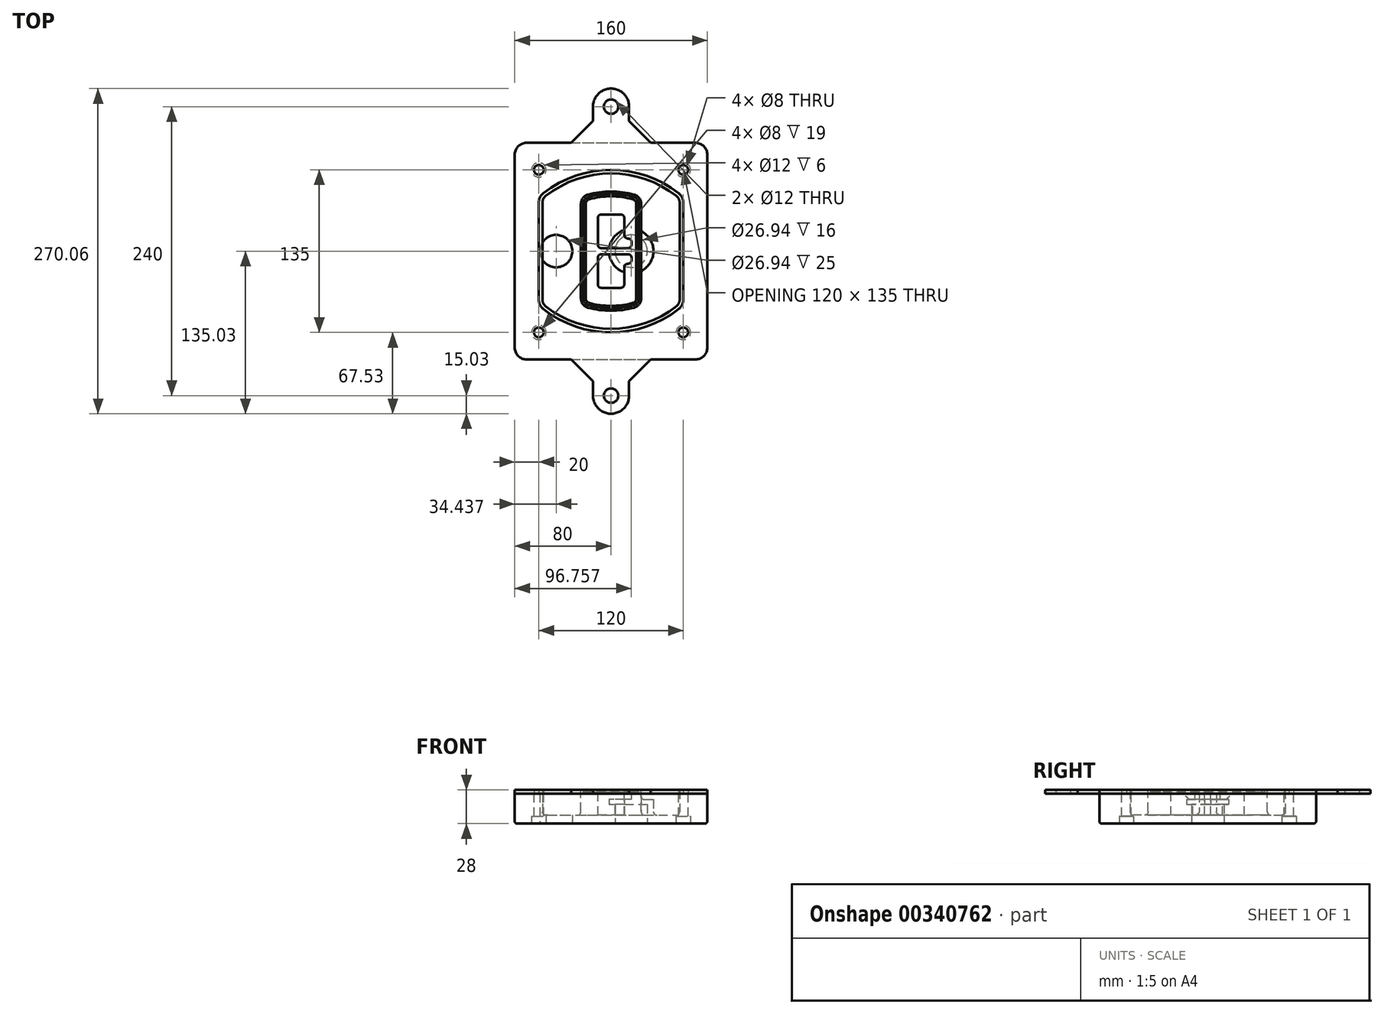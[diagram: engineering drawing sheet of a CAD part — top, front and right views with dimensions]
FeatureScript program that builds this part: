
annotation { "Feature Type Name" : "Feature", "Feature Type Description" : "" }
export const myFeature = defineFeature(function(context is Context, id is Id, definition is map)
    precondition{}
    {
        {
            var Q0;
            Q0=qCreatedBy(makeId("Top.planeOp"),FACE);
            var sketch = newSketch(context, id + "F0", { "sketchPlane" : qUnion([Q0])});
            skPoint(sketch, "E0.rect.middle", {"position": v(0, 0) * mm});
            skLineSegment(sketch, "E1.bottom", {"start": v(-70, -90) * mm, "end": v(70, -90) * mm});
            skLineSegment(sketch, "E1.top", {"start": v(-70, 90) * mm, "end": v(70, 90) * mm});
            skLineSegment(sketch, "E1.left", {"start": v(-80, -80) * mm, "end": v(-80, 80) * mm});
            skLineSegment(sketch, "E1.right", {"start": v(80, -80) * mm, "end": v(80, 80) * mm});
            skLineSegment(sketch, "E2", {"start": v(-80, 90) * mm, "end": v(80, -90) * mm, "construction": true});
            skLineSegment(sketch, "E3", {"start": v(80, 90) * mm, "end": v(-80, -90) * mm, "construction": true});
            skCircle(sketch, "E4", {"center": v(-60, 67.5) * mm, "radius": 4 * mm});
            skCircle(sketch, "E5", {"center": v(60, 67.5) * mm, "radius": 4 * mm});
            skCircle(sketch, "E6", {"center": v(60, -67.5) * mm, "radius": 4 * mm});
            skCircle(sketch, "E7", {"center": v(-60, -67.5) * mm, "radius": 4 * mm});
            skLineSegment(sketch, "E8", {"start": v(-60, 67.5) * mm, "end": v(60, 67.5) * mm, "construction": true});
            skLineSegment(sketch, "E9", {"start": v(60, 67.5) * mm, "end": v(60, -67.5) * mm, "construction": true});
            skLineSegment(sketch, "E10", {"start": v(60, -67.5) * mm, "end": v(-60, -67.5) * mm, "construction": true});
            skLineSegment(sketch, "E11", {"start": v(-60, -67.5) * mm, "end": v(-60, 67.5) * mm, "construction": true});
            skLineSegment(sketch, "E12", {"start": v(-60, 40.3) * mm, "end": v(-60, -40.3) * mm});
            skLineSegment(sketch, "E13", {"start": v(60, 40.3) * mm, "end": v(60, -40.3) * mm});
            skArc(sketch, "E14", {"start": v(56.15, 48.18) * mm, "mid": v(0, 67.5) * mm, "end": v(-56.15, 48.18) * mm});
            skArc(sketch, "E15", {"start": v(-56.15, -48.18) * mm, "mid": v(0, -67.5) * mm, "end": v(56.15, -48.18) * mm});
            skLineSegment(sketch, "E16", {"start": v(-60, 0) * mm, "end": v(60, 0) * mm, "construction": true});
            skPoint(sketch, "E17.visualSharp", {"position": v(-60, -45) * mm});
            skArc(sketch, "E17.filletArc", {"start": v(-60, -40.3) * mm, "mid": v(-58.99, -44.68) * mm, "end": v(-56.15, -48.18) * mm});
            skPoint(sketch, "E18.visualSharp", {"position": v(-60, 45) * mm});
            skArc(sketch, "E18.filletArc", {"start": v(-56.15, 48.18) * mm, "mid": v(-58.99, 44.68) * mm, "end": v(-60, 40.3) * mm});
            skPoint(sketch, "E19.visualSharp", {"position": v(60, 45) * mm});
            skArc(sketch, "E19.filletArc", {"start": v(60, 40.3) * mm, "mid": v(58.99, 44.68) * mm, "end": v(56.15, 48.18) * mm});
            skPoint(sketch, "E20.visualSharp", {"position": v(60, -45) * mm});
            skArc(sketch, "E20.filletArc", {"start": v(56.15, -48.18) * mm, "mid": v(58.99, -44.68) * mm, "end": v(60, -40.3) * mm});
            skPoint(sketch, "E21.visualSharp", {"position": v(-80, 90) * mm});
            skArc(sketch, "E21.filletArc", {"start": v(-70, 90) * mm, "mid": v(-77.07, 87.07) * mm, "end": v(-80, 80) * mm});
            skPoint(sketch, "E22.visualSharp", {"position": v(80, 90) * mm});
            skArc(sketch, "E22.filletArc", {"start": v(80, 80) * mm, "mid": v(77.07, 87.07) * mm, "end": v(70, 90) * mm});
            skPoint(sketch, "E23.visualSharp", {"position": v(80, -90) * mm});
            skArc(sketch, "E23.filletArc", {"start": v(70, -90) * mm, "mid": v(77.07, -87.07) * mm, "end": v(80, -80) * mm});
            skPoint(sketch, "E24.visualSharp", {"position": v(-80, -90) * mm});
            skArc(sketch, "E24.filletArc", {"start": v(-80, -80) * mm, "mid": v(-77.07, -87.07) * mm, "end": v(-70, -90) * mm});
            skArc(sketch, "E25.0", {"start": v(57, 40.3) * mm, "mid": v(56.3, 43.36) * mm, "end": v(54.3, 45.81) * mm});
            skLineSegment(sketch, "E25.1", {"start": v(57, 40.3) * mm, "end": v(57, -40.3) * mm});
            skArc(sketch, "E25.2", {"start": v(54.3, -45.81) * mm, "mid": v(56.3, -43.36) * mm, "end": v(57, -40.3) * mm});
            skArc(sketch, "E25.3", {"start": v(-54.3, -45.81) * mm, "mid": v(0, -64.5) * mm, "end": v(54.3, -45.81) * mm});
            skArc(sketch, "E25.4", {"start": v(-57, -40.3) * mm, "mid": v(-56.3, -43.36) * mm, "end": v(-54.3, -45.81) * mm});
            skArc(sketch, "E25.5", {"start": v(54.3, 45.81) * mm, "mid": v(0, 64.5) * mm, "end": v(-54.3, 45.81) * mm});
            skLineSegment(sketch, "E25.6", {"start": v(-57, 40.3) * mm, "end": v(-57, -40.3) * mm});
            skArc(sketch, "E25.7", {"start": v(-54.3, 45.81) * mm, "mid": v(-56.3, 43.36) * mm, "end": v(-57, 40.3) * mm});
            skArc(sketch, "E26.0", {"start": v(-58.62, 51.33) * mm, "mid": v(-62.58, 46.43) * mm, "end": v(-64, 40.3) * mm});
            skArc(sketch, "E26.1", {"start": v(58.62, 51.33) * mm, "mid": v(0, 71.5) * mm, "end": v(-58.62, 51.33) * mm});
            skArc(sketch, "E26.2", {"start": v(64, 40.3) * mm, "mid": v(62.58, 46.43) * mm, "end": v(58.62, 51.33) * mm});
            skLineSegment(sketch, "E26.3", {"start": v(64, 40.3) * mm, "end": v(64, -40.3) * mm});
            skArc(sketch, "E26.4", {"start": v(58.62, -51.33) * mm, "mid": v(62.58, -46.43) * mm, "end": v(64, -40.3) * mm});
            skLineSegment(sketch, "E26.5", {"start": v(-64, 40.3) * mm, "end": v(-64, -40.3) * mm});
            skArc(sketch, "E26.6", {"start": v(-58.62, -51.33) * mm, "mid": v(0, -71.5) * mm, "end": v(58.62, -51.33) * mm});
            skArc(sketch, "E26.7", {"start": v(-64, -40.3) * mm, "mid": v(-62.58, -46.43) * mm, "end": v(-58.62, -51.33) * mm});
            skSolve(sketch);
        }
        {
            var Q0;
            Q0=makeQuery(id+"F0.imprint","IMPRINT",FACE,{"disambiguationData":[TD([[makeQuery(id+"F0.imprint","IMPRINT",EDGE,{"derivedFrom":sQuery(id+"F0.wireOp",EDGE,"E1.bottom")}),1.0]])]});
            var Q1;
            Q1=makeQuery(id+"F0.imprint","IMPRINT",FACE,{"disambiguationData":[TD([[makeQuery(id+"F0.imprint","IMPRINT",EDGE,{"derivedFrom":sQuery(id+"F0.wireOp",EDGE,"E12")}),1.0]])]});
            var Q2;
            Q2=makeQuery(id+"F0.imprint","IMPRINT",FACE,{"disambiguationData":[TD([[makeQuery(id+"F0.imprint","IMPRINT",EDGE,{"derivedFrom":sQuery(id+"F0.wireOp",EDGE,"E25.0")}),1.0]])]});
            var Q3;
            Q3=makeQuery(id+"F0.imprint","IMPRINT",FACE,{"disambiguationData":[TD([[makeQuery(id+"F0.imprint","IMPRINT",EDGE,{"derivedFrom":sQuery(id+"F0.wireOp",EDGE,"E12")}),-1.0]])]});
            extrude(context, id + "F1", {"entities" : qUnion([Q0, Q1, Q2, Q3]), "oppositeDirection" : true, "depth" : 25 * mm});
        }
        {
            var Q0;
            Q0=makeQuery(id+"F0.imprint","IMPRINT",FACE,{"disambiguationData":[TD([[makeQuery(id+"F0.imprint","IMPRINT",EDGE,{"derivedFrom":sQuery(id+"F0.wireOp",EDGE,"E12")}),1.0]])]});
            extrude(context, id + "F2", {"entities" : qUnion([Q0]), "operationType" : NewBodyOperationType.ADD, "depth" : 3 * mm});
        }
        {
            var Q0;
            Q0=makeQuery(id+"F0.imprint","IMPRINT",FACE,{"disambiguationData":[TD([[makeQuery(id+"F0.imprint","IMPRINT",EDGE,{"derivedFrom":sQuery(id+"F0.wireOp",EDGE,"E25.0")}),1.0]])]});
            extrude(context, id + "F3", {"entities" : qUnion([Q0]), "operationType" : NewBodyOperationType.REMOVE, "oppositeDirection" : true, "depth" : 18 * mm});
        }
        {
            var Q0;
            Q0=makeQuery(id+"F2.opExtrude","CAP_FACE",FACE,{"disambiguationData":[OSD([sQuery(id+"F0.wireOp",EDGE,"E12"),sQuery(id+"F0.wireOp",EDGE,"E13"),sQuery(id+"F0.wireOp",EDGE,"E14"),sQuery(id+"F0.wireOp",EDGE,"E15"),sQuery(id+"F0.wireOp",EDGE,"E17.filletArc"),sQuery(id+"F0.wireOp",EDGE,"E18.filletArc"),sQuery(id+"F0.wireOp",EDGE,"E19.filletArc"),sQuery(id+"F0.wireOp",EDGE,"E20.filletArc"),sQuery(id+"F0.wireOp",EDGE,"E25.0"),sQuery(id+"F0.wireOp",EDGE,"E25.1"),sQuery(id+"F0.wireOp",EDGE,"E25.2"),sQuery(id+"F0.wireOp",EDGE,"E25.3"),sQuery(id+"F0.wireOp",EDGE,"E25.4"),sQuery(id+"F0.wireOp",EDGE,"E25.5"),sQuery(id+"F0.wireOp",EDGE,"E25.6"),sQuery(id+"F0.wireOp",EDGE,"E25.7")])],"isStart":false});
            var sketch = newSketch(context, id + "F4", { "sketchPlane" : qUnion([Q0])});
            skArc(sketch, "E27.0", {"start": v(-19.08, -46.97) * mm, "mid": v(0, -49.5) * mm, "end": v(19.08, -46.97) * mm});
            skArc(sketch, "E28.0", {"start": v(19.08, 46.97) * mm, "mid": v(0, 49.5) * mm, "end": v(-19.08, 46.97) * mm});
            skLineSegment(sketch, "E29", {"start": v(-25, 39.25) * mm, "end": v(-25, -39.25) * mm});
            skLineSegment(sketch, "E30", {"start": v(25, 39.25) * mm, "end": v(25, -39.25) * mm});
            skLineSegment(sketch, "E31", {"start": v(-25, 45.1) * mm, "end": v(25, 45.1) * mm, "construction": true});
            skLineSegment(sketch, "E32", {"start": v(-25, -45.1) * mm, "end": v(25, -45.1) * mm, "construction": true});
            skPoint(sketch, "E33.visualSharp", {"position": v(-25, 45.1) * mm});
            skArc(sketch, "E33.filletArc", {"start": v(-19.08, 46.97) * mm, "mid": v(-23.35, 44.11) * mm, "end": v(-25, 39.25) * mm});
            skPoint(sketch, "E34.visualSharp", {"position": v(25, 45.1) * mm});
            skArc(sketch, "E34.filletArc", {"start": v(25, 39.25) * mm, "mid": v(23.35, 44.11) * mm, "end": v(19.08, 46.97) * mm});
            skPoint(sketch, "E35.visualSharp", {"position": v(25, -45.1) * mm});
            skArc(sketch, "E35.filletArc", {"start": v(19.08, -46.97) * mm, "mid": v(23.35, -44.11) * mm, "end": v(25, -39.25) * mm});
            skPoint(sketch, "E36.visualSharp", {"position": v(-25, -45.1) * mm});
            skArc(sketch, "E36.filletArc", {"start": v(-25, -39.25) * mm, "mid": v(-23.35, -44.11) * mm, "end": v(-19.08, -46.97) * mm});
            skArc(sketch, "E37.0", {"start": v(54.3, 45.81) * mm, "mid": v(0, 64.5) * mm, "end": v(-54.3, 45.81) * mm});
            skArc(sketch, "E37.1", {"start": v(-54.3, 45.81) * mm, "mid": v(-56.3, 43.36) * mm, "end": v(-57, 40.3) * mm});
            skLineSegment(sketch, "E37.2", {"start": v(-57, 40.3) * mm, "end": v(-57, -40.3) * mm});
            skArc(sketch, "E37.3", {"start": v(-57, -40.3) * mm, "mid": v(-56.3, -43.36) * mm, "end": v(-54.3, -45.81) * mm});
            skArc(sketch, "E37.4", {"start": v(-54.3, -45.81) * mm, "mid": v(0, -64.5) * mm, "end": v(54.3, -45.81) * mm});
            skArc(sketch, "E37.5", {"start": v(54.3, -45.81) * mm, "mid": v(56.3, -43.36) * mm, "end": v(57, -40.3) * mm});
            skLineSegment(sketch, "E37.6", {"start": v(57, 40.3) * mm, "end": v(57, -40.3) * mm});
            skArc(sketch, "E37.7", {"start": v(57, 40.3) * mm, "mid": v(56.3, 43.36) * mm, "end": v(54.3, 45.81) * mm});
            skLineSegment(sketch, "E38.0", {"start": v(23, 39.25) * mm, "end": v(23, -39.25) * mm});
            skArc(sketch, "E38.1", {"start": v(18.56, -45.04) * mm, "mid": v(21.76, -42.9) * mm, "end": v(23, -39.25) * mm});
            skArc(sketch, "E38.2", {"start": v(-18.56, -45.04) * mm, "mid": v(0, -47.5) * mm, "end": v(18.56, -45.04) * mm});
            skArc(sketch, "E38.3", {"start": v(-23, -39.25) * mm, "mid": v(-21.76, -42.9) * mm, "end": v(-18.56, -45.04) * mm});
            skLineSegment(sketch, "E38.4", {"start": v(-23, 39.25) * mm, "end": v(-23, -39.25) * mm});
            skArc(sketch, "E38.5", {"start": v(23, 39.25) * mm, "mid": v(21.76, 42.9) * mm, "end": v(18.56, 45.04) * mm});
            skArc(sketch, "E38.6", {"start": v(-18.56, 45.04) * mm, "mid": v(-21.76, 42.9) * mm, "end": v(-23, 39.25) * mm});
            skArc(sketch, "E38.7", {"start": v(18.56, 45.04) * mm, "mid": v(0, 47.5) * mm, "end": v(-18.56, 45.04) * mm});
            skArc(sketch, "E39.0", {"start": v(21, 39.25) * mm, "mid": v(20.18, 41.68) * mm, "end": v(18.04, 43.1) * mm});
            skLineSegment(sketch, "E39.1", {"start": v(21, 39.25) * mm, "end": v(21, -39.25) * mm});
            skArc(sketch, "E39.2", {"start": v(18.04, -43.1) * mm, "mid": v(20.18, -41.68) * mm, "end": v(21, -39.25) * mm});
            skArc(sketch, "E39.3", {"start": v(-18.04, -43.1) * mm, "mid": v(0, -45.5) * mm, "end": v(18.04, -43.1) * mm});
            skArc(sketch, "E39.4", {"start": v(-21, -39.25) * mm, "mid": v(-20.18, -41.68) * mm, "end": v(-18.04, -43.1) * mm});
            skArc(sketch, "E39.5", {"start": v(18.04, 43.1) * mm, "mid": v(0, 45.5) * mm, "end": v(-18.04, 43.1) * mm});
            skLineSegment(sketch, "E39.6", {"start": v(-21, 39.25) * mm, "end": v(-21, -39.25) * mm});
            skArc(sketch, "E39.7", {"start": v(-18.04, 43.1) * mm, "mid": v(-20.18, 41.68) * mm, "end": v(-21, 39.25) * mm});
            skLineSegment(sketch, "E40", {"start": v(-25, 0) * mm, "end": v(25, 0) * mm, "construction": true});
            skLineSegment(sketch, "E41", {"start": v(-11, 5.5) * mm, "end": v(-11, 27.5) * mm});
            skLineSegment(sketch, "E42", {"start": v(-8, 30.5) * mm, "end": v(8, 30.5) * mm});
            skLineSegment(sketch, "E43", {"start": v(11, 27.5) * mm, "end": v(11, 13.5) * mm});
            skLineSegment(sketch, "E44", {"start": v(14, 10.5) * mm, "end": v(14, 10.5) * mm});
            skLineSegment(sketch, "E45", {"start": v(17, 7.5) * mm, "end": v(17, 5.5) * mm});
            skLineSegment(sketch, "E46", {"start": v(14, 2.5) * mm, "end": v(-8, 2.5) * mm});
            skPoint(sketch, "E47.visualSharp", {"position": v(-11, 30.5) * mm});
            skArc(sketch, "E47.filletArc", {"start": v(-8, 30.5) * mm, "mid": v(-10.12, 29.62) * mm, "end": v(-11, 27.5) * mm});
            skPoint(sketch, "E48.visualSharp", {"position": v(11, 30.5) * mm});
            skArc(sketch, "E48.filletArc", {"start": v(11, 27.5) * mm, "mid": v(10.12, 29.62) * mm, "end": v(8, 30.5) * mm});
            skPoint(sketch, "E49.visualSharp", {"position": v(11, 10.5) * mm});
            skArc(sketch, "E49.filletArc", {"start": v(11, 13.5) * mm, "mid": v(11.88, 11.38) * mm, "end": v(14, 10.5) * mm});
            skPoint(sketch, "E50.visualSharp", {"position": v(17, 10.5) * mm});
            skArc(sketch, "E50.filletArc", {"start": v(17, 7.5) * mm, "mid": v(16.12, 9.62) * mm, "end": v(14, 10.5) * mm});
            skPoint(sketch, "E51.visualSharp", {"position": v(17, 2.5) * mm});
            skArc(sketch, "E51.filletArc", {"start": v(14, 2.5) * mm, "mid": v(16.12, 3.38) * mm, "end": v(17, 5.5) * mm});
            skPoint(sketch, "E52.visualSharp", {"position": v(-11, 2.5) * mm});
            skArc(sketch, "E52.filletArc", {"start": v(-11, 5.5) * mm, "mid": v(-10.12, 3.38) * mm, "end": v(-8, 2.5) * mm});
            skLineSegment(sketch, "E53.0.MirrorCS", {"start": v(14, -2.5) * mm, "end": v(-8, -2.5) * mm});
            skArc(sketch, "E54.0.MirrorCS", {"start": v(-11, -5.5) * mm, "mid": v(-10.12, -3.38) * mm, "end": v(-8, -2.5) * mm});
            skLineSegment(sketch, "E55.0.MirrorCS", {"start": v(-11, -5.5) * mm, "end": v(-11, -27.5) * mm});
            skArc(sketch, "E56.0.MirrorCS", {"start": v(-8, -30.5) * mm, "mid": v(-10.12, -29.62) * mm, "end": v(-11, -27.5) * mm});
            skLineSegment(sketch, "E57.0.MirrorCS", {"start": v(-8, -30.5) * mm, "end": v(8, -30.5) * mm});
            skArc(sketch, "E58.0.MirrorCS", {"start": v(11, -27.5) * mm, "mid": v(10.12, -29.62) * mm, "end": v(8, -30.5) * mm});
            skLineSegment(sketch, "E59.0.MirrorCS", {"start": v(11, -27.5) * mm, "end": v(11, -13.5) * mm});
            skArc(sketch, "E60.0.MirrorCS", {"start": v(11, -13.5) * mm, "mid": v(11.88, -11.38) * mm, "end": v(14, -10.5) * mm});
            skArc(sketch, "E61.0.MirrorCS", {"start": v(17, -7.5) * mm, "mid": v(16.12, -9.62) * mm, "end": v(14, -10.5) * mm});
            skLineSegment(sketch, "E62.0.MirrorCS", {"start": v(17, -7.5) * mm, "end": v(17, -5.5) * mm});
            skArc(sketch, "E63.0.MirrorCS", {"start": v(14, -2.5) * mm, "mid": v(16.12, -3.38) * mm, "end": v(17, -5.5) * mm});
            skSolve(sketch);
        }
        {
            var Q0;
            Q0=makeQuery(id+"F4.imprint","IMPRINT",FACE,{"disambiguationData":[TD([[makeQuery(id+"F4.imprint","IMPRINT",EDGE,{"derivedFrom":sQuery(id+"F4.wireOp",EDGE,"E27.0")}),1.0]])]});
            var Q1;
            Q1=makeQuery(id+"F4.imprint","IMPRINT",FACE,{"disambiguationData":[TD([[makeQuery(id+"F4.imprint","IMPRINT",EDGE,{"derivedFrom":sQuery(id+"F4.wireOp",EDGE,"E38.0")}),-1.0]])]});
            var Q2;
            Q2=makeQuery(id+"F4.imprint","IMPRINT",FACE,{"disambiguationData":[TD([[makeQuery(id+"F4.imprint","IMPRINT",EDGE,{"derivedFrom":sQuery(id+"F4.wireOp",EDGE,"E39.0")}),1.0]])]});
            extrude(context, id + "F5", {"entities" : qUnion([Q0, Q1, Q2]), "operationType" : NewBodyOperationType.ADD, "endBound" : BoundingType.UP_TO_NEXT, "oppositeDirection" : true, "depth" : 25 * mm});
        }
        {
            var Q0;
            Q0=makeQuery(id+"F4.imprint","IMPRINT",FACE,{"disambiguationData":[TD([[makeQuery(id+"F4.imprint","IMPRINT",EDGE,{"derivedFrom":sQuery(id+"F4.wireOp",EDGE,"E38.0")}),-1.0]])]});
            extrude(context, id + "F6", {"entities" : qUnion([Q0]), "operationType" : NewBodyOperationType.REMOVE, "oppositeDirection" : true, "depth" : 2 * mm});
        }
        {
            var Q0;
            Q0=makeQuery(id+"F1.opExtrude","CAP_FACE",FACE,{"disambiguationData":[OSD([sQuery(id+"F0.wireOp",EDGE,"E1.bottom"),sQuery(id+"F0.wireOp",EDGE,"E1.top"),sQuery(id+"F0.wireOp",EDGE,"E1.left"),sQuery(id+"F0.wireOp",EDGE,"E1.right"),sQuery(id+"F0.wireOp",EDGE,"E4"),sQuery(id+"F0.wireOp",EDGE,"E5"),sQuery(id+"F0.wireOp",EDGE,"E6"),sQuery(id+"F0.wireOp",EDGE,"E7"),sQuery(id+"F0.wireOp",EDGE,"E21.filletArc"),sQuery(id+"F0.wireOp",EDGE,"E22.filletArc"),sQuery(id+"F0.wireOp",EDGE,"E23.filletArc"),sQuery(id+"F0.wireOp",EDGE,"E24.filletArc")])],"isStart":false});
            var sketch = newSketch(context, id + "F7", { "sketchPlane" : qUnion([Q0])});
            skCircle(sketch, "E64", {"center": v(16.76, 0) * mm, "radius": 13.47 * mm});
            skCircle(sketch, "E65", {"center": v(-45.56, 0) * mm, "radius": 13.47 * mm});
            skLineSegment(sketch, "E66", {"start": v(80, 0) * mm, "end": v(-80, 0) * mm});
            skCircle(sketch, "E67", {"center": v(16.76, 0) * mm, "radius": 18.47 * mm});
            skCircle(sketch, "E68", {"center": v(60, -67.5) * mm, "radius": 6 * mm});
            skCircle(sketch, "E69", {"center": v(-60, -67.5) * mm, "radius": 6 * mm});
            skCircle(sketch, "E70", {"center": v(-60, 67.5) * mm, "radius": 6 * mm});
            skCircle(sketch, "E71", {"center": v(60, 67.5) * mm, "radius": 6 * mm});
            skSolve(sketch);
        }
        {
            var Q0;
            {var subQ1=sQuery(id+"F7.wireOp",EDGE,"E66");var subQ4=sQuery(id+"F7.wireOp",EDGE,"E64");var subQ6=makeQuery(id+"F7.imprint","INTERSECT",VERTEX,{"disambiguationData":[OD(0.0)],"derivedFrom":[subQ4,subQ1]});Q0=makeQuery(id+"F7.imprint","IMPRINT",FACE,{"disambiguationData":[TD([[makeQuery(id+"F7.imprint","IMPRINT",EDGE,{"disambiguationData":[TD([[subQ6,-1.0]])],"derivedFrom":subQ4}),-1.0]])]});}
            var Q1;
            {var subQ0=sQuery(id+"F7.wireOp",EDGE,"E66");var subQ1=sQuery(id+"F7.wireOp",EDGE,"E64");var subQ3=makeQuery(id+"F7.imprint","INTERSECT",VERTEX,{"disambiguationData":[OD(0.0)],"derivedFrom":[subQ1,subQ0]});Q1=makeQuery(id+"F7.imprint","IMPRINT",FACE,{"disambiguationData":[TD([[makeQuery(id+"F7.imprint","IMPRINT",EDGE,{"disambiguationData":[TD([[subQ3,-1.0]])],"derivedFrom":subQ1}),1.0]])]});}
            var Q2;
            {var subQ0=sQuery(id+"F7.wireOp",EDGE,"E66");var subQ1=sQuery(id+"F7.wireOp",EDGE,"E64");var subQ3=makeQuery(id+"F7.imprint","INTERSECT",VERTEX,{"disambiguationData":[OD(0.0)],"derivedFrom":[subQ1,subQ0]});Q2=makeQuery(id+"F7.imprint","IMPRINT",FACE,{"disambiguationData":[TD([[makeQuery(id+"F7.imprint","IMPRINT",EDGE,{"disambiguationData":[TD([[subQ3,1.0]])],"derivedFrom":subQ1}),1.0]])]});}
            var Q3;
            {var subQ1=sQuery(id+"F7.wireOp",EDGE,"E66");var subQ4=sQuery(id+"F7.wireOp",EDGE,"E64");var subQ6=makeQuery(id+"F7.imprint","INTERSECT",VERTEX,{"disambiguationData":[OD(0.0)],"derivedFrom":[subQ4,subQ1]});Q3=makeQuery(id+"F7.imprint","IMPRINT",FACE,{"disambiguationData":[TD([[makeQuery(id+"F7.imprint","IMPRINT",EDGE,{"disambiguationData":[TD([[subQ6,1.0]])],"derivedFrom":subQ4}),-1.0]])]});}
            extrude(context, id + "F8", {"entities" : qUnion([Q0, Q1, Q2, Q3]), "operationType" : NewBodyOperationType.ADD, "oppositeDirection" : true, "depth" : 20 * mm});
        }
        {
            var Q0;
            {var subQ0=sQuery(id+"F7.wireOp",EDGE,"E66");var subQ1=sQuery(id+"F7.wireOp",EDGE,"E64");var subQ3=makeQuery(id+"F7.imprint","INTERSECT",VERTEX,{"disambiguationData":[OD(0.0)],"derivedFrom":[subQ1,subQ0]});Q0=makeQuery(id+"F7.imprint","IMPRINT",FACE,{"disambiguationData":[TD([[makeQuery(id+"F7.imprint","IMPRINT",EDGE,{"disambiguationData":[TD([[subQ3,-1.0]])],"derivedFrom":subQ1}),1.0]])]});}
            var Q1;
            {var subQ0=sQuery(id+"F7.wireOp",EDGE,"E66");var subQ1=sQuery(id+"F7.wireOp",EDGE,"E64");var subQ3=makeQuery(id+"F7.imprint","INTERSECT",VERTEX,{"disambiguationData":[OD(0.0)],"derivedFrom":[subQ1,subQ0]});Q1=makeQuery(id+"F7.imprint","IMPRINT",FACE,{"disambiguationData":[TD([[makeQuery(id+"F7.imprint","IMPRINT",EDGE,{"disambiguationData":[TD([[subQ3,1.0]])],"derivedFrom":subQ1}),1.0]])]});}
            extrude(context, id + "F9", {"entities" : qUnion([Q0, Q1]), "operationType" : NewBodyOperationType.REMOVE, "oppositeDirection" : true, "depth" : 16 * mm});
        }
        {
            var Q0;
            {var subQ0=sQuery(id+"F7.wireOp",EDGE,"E66");var subQ1=sQuery(id+"F7.wireOp",EDGE,"E65");var subQ3=makeQuery(id+"F7.imprint","INTERSECT",VERTEX,{"disambiguationData":[OD(0.0)],"derivedFrom":[subQ1,subQ0]});Q0=makeQuery(id+"F7.imprint","IMPRINT",FACE,{"disambiguationData":[TD([[makeQuery(id+"F7.imprint","IMPRINT",EDGE,{"disambiguationData":[TD([[subQ3,-1.0]])],"derivedFrom":subQ1}),1.0]])]});}
            var Q1;
            {var subQ0=sQuery(id+"F7.wireOp",EDGE,"E66");var subQ1=sQuery(id+"F7.wireOp",EDGE,"E65");var subQ3=makeQuery(id+"F7.imprint","INTERSECT",VERTEX,{"disambiguationData":[OD(0.0)],"derivedFrom":[subQ1,subQ0]});Q1=makeQuery(id+"F7.imprint","IMPRINT",FACE,{"disambiguationData":[TD([[makeQuery(id+"F7.imprint","IMPRINT",EDGE,{"disambiguationData":[TD([[subQ3,1.0]])],"derivedFrom":subQ1}),1.0]])]});}
            extrude(context, id + "F10", {"entities" : qUnion([Q0, Q1]), "operationType" : NewBodyOperationType.REMOVE, "oppositeDirection" : true, "depth" : 25 * mm});
        }
        {
            var Q0;
            Q0=makeQuery(id+"F7.imprint","IMPRINT",FACE,{"disambiguationData":[TD([[makeQuery(id+"F7.imprint","IMPRINT",EDGE,{"derivedFrom":sQuery(id+"F7.wireOp",EDGE,"E68")}),1.0]])]});
            var Q1;
            Q1=makeQuery(id+"F7.imprint","IMPRINT",FACE,{"disambiguationData":[TD([[makeQuery(id+"F7.imprint","IMPRINT",EDGE,{"derivedFrom":makeQuery(id+"F1.opExtrude","CAP_EDGE",EDGE,{"disambiguationData":[OSD([sQuery(id+"F0.wireOp",EDGE,"E5")])],"isStart":false})}),-1.0]])]});
            var Q2;
            Q2=makeQuery(id+"F7.imprint","IMPRINT",FACE,{"disambiguationData":[TD([[makeQuery(id+"F7.imprint","IMPRINT",EDGE,{"derivedFrom":sQuery(id+"F7.wireOp",EDGE,"E69")}),1.0]])]});
            var Q3;
            Q3=makeQuery(id+"F7.imprint","IMPRINT",FACE,{"disambiguationData":[TD([[makeQuery(id+"F7.imprint","IMPRINT",EDGE,{"derivedFrom":makeQuery(id+"F1.opExtrude","CAP_EDGE",EDGE,{"disambiguationData":[OSD([sQuery(id+"F0.wireOp",EDGE,"E4")])],"isStart":false})}),-1.0]])]});
            var Q4;
            Q4=makeQuery(id+"F7.imprint","IMPRINT",FACE,{"disambiguationData":[TD([[makeQuery(id+"F7.imprint","IMPRINT",EDGE,{"derivedFrom":sQuery(id+"F7.wireOp",EDGE,"E70")}),1.0]])]});
            var Q5;
            Q5=makeQuery(id+"F7.imprint","IMPRINT",FACE,{"disambiguationData":[TD([[makeQuery(id+"F7.imprint","IMPRINT",EDGE,{"derivedFrom":makeQuery(id+"F1.opExtrude","CAP_EDGE",EDGE,{"disambiguationData":[OSD([sQuery(id+"F0.wireOp",EDGE,"E7")])],"isStart":false})}),-1.0]])]});
            var Q6;
            Q6=makeQuery(id+"F7.imprint","IMPRINT",FACE,{"disambiguationData":[TD([[makeQuery(id+"F7.imprint","IMPRINT",EDGE,{"derivedFrom":sQuery(id+"F7.wireOp",EDGE,"E71")}),1.0]])]});
            var Q7;
            Q7=makeQuery(id+"F7.imprint","IMPRINT",FACE,{"disambiguationData":[TD([[makeQuery(id+"F7.imprint","IMPRINT",EDGE,{"derivedFrom":makeQuery(id+"F1.opExtrude","CAP_EDGE",EDGE,{"disambiguationData":[OSD([sQuery(id+"F0.wireOp",EDGE,"E6")])],"isStart":false})}),-1.0]])]});
            extrude(context, id + "F11", {"entities" : qUnion([Q0, Q1, Q2, Q3, Q4, Q5, Q6, Q7]), "operationType" : NewBodyOperationType.REMOVE, "oppositeDirection" : true, "depth" : 6 * mm});
        }
        {
            var Q0;
            Q0=makeQuery(id+"F9.boolean.opBoolean","COPY",FACE,{"derivedFrom":makeQuery(id+"F9.opExtrude","CAP_FACE",FACE,{"disambiguationData":[OSD([sQuery(id+"F7.wireOp",EDGE,"E64")])],"isStart":false})});
            var sketch = newSketch(context, id + "F12", { "sketchPlane" : qUnion([Q0])});
            skArc(sketch, "E72.0", {"start": v(11, 17.55) * mm, "mid": v(2.57, 11.82) * mm, "end": v(-1.54, 2.5) * mm});
            skArc(sketch, "E72.1", {"start": v(-1.54, -2.5) * mm, "mid": v(2.57, -11.82) * mm, "end": v(11, -17.55) * mm});
            skLineSegment(sketch, "E73", {"start": v(-1.54, -2.5) * mm, "end": v(14, -2.5) * mm});
            skLineSegment(sketch, "E74.0", {"start": v(14, 2.5) * mm, "end": v(-1.54, 2.5) * mm});
            skArc(sketch, "E74.1", {"start": v(14, 2.5) * mm, "mid": v(16.12, 3.38) * mm, "end": v(17, 5.5) * mm});
            skLineSegment(sketch, "E74.2", {"start": v(17, 7.5) * mm, "end": v(17, 5.5) * mm});
            skArc(sketch, "E74.3", {"start": v(17, 7.5) * mm, "mid": v(16.12, 9.62) * mm, "end": v(14, 10.5) * mm});
            skArc(sketch, "E74.4", {"start": v(11, 13.5) * mm, "mid": v(11.88, 11.38) * mm, "end": v(14, 10.5) * mm});
            skLineSegment(sketch, "E74.5", {"start": v(11, 17.55) * mm, "end": v(11, 13.5) * mm});
            skLineSegment(sketch, "E74.7", {"start": v(14, -2.5) * mm, "end": v(-1.54, -2.5) * mm});
            skArc(sketch, "E74.8", {"start": v(14, -2.5) * mm, "mid": v(16.12, -3.38) * mm, "end": v(17, -5.5) * mm});
            skLineSegment(sketch, "E74.9", {"start": v(17, -7.5) * mm, "end": v(17, -5.5) * mm});
            skArc(sketch, "E74.10", {"start": v(17, -7.5) * mm, "mid": v(16.12, -9.62) * mm, "end": v(14, -10.5) * mm});
            skArc(sketch, "E74.11", {"start": v(11, -13.5) * mm, "mid": v(11.88, -11.38) * mm, "end": v(14, -10.5) * mm});
            skLineSegment(sketch, "E74.12", {"start": v(11, -17.55) * mm, "end": v(11, -13.5) * mm});
            skPoint(sketch, "E75.orphan", {"position": v(11, -27.5) * mm});
            skPoint(sketch, "E76.orphan", {"position": v(-8, -2.5) * mm});
            skPoint(sketch, "E77.orphan", {"position": v(-8, 2.5) * mm});
            skPoint(sketch, "E78.orphan", {"position": v(11, 27.5) * mm});
            skSolve(sketch);
        }
        {
            var Q0;
            {var subQ7=sQuery(id+"F12.wireOp",EDGE,"E72.0");var subQ14=sQuery(id+"F12.wireOp",EDGE,"E72.1");var subQ16=sQuery(id+"F12.wireOp",EDGE,"E74.1");var subQ18=sQuery(id+"F12.wireOp",EDGE,"E74.8");Q0=qUnion([makeQuery(id+"F12.imprint","IMPRINT",FACE,{"disambiguationData":[TD([[makeQuery(id+"F12.imprint","IMPRINT",EDGE,{"derivedFrom":subQ7}),1.0]])]}),makeQuery(id+"F12.imprint","IMPRINT",FACE,{"disambiguationData":[TD([[makeQuery(id+"F12.imprint","IMPRINT",EDGE,{"derivedFrom":subQ14}),1.0]])]}),makeQuery(id+"F12.imprint","IMPRINT",FACE,{"disambiguationData":[TD([[makeQuery(id+"F12.imprint","IMPRINT",EDGE,{"derivedFrom":subQ16}),1.0]])]}),makeQuery(id+"F12.imprint","IMPRINT",FACE,{"disambiguationData":[TD([[makeQuery(id+"F12.imprint","IMPRINT",EDGE,{"derivedFrom":subQ18}),-1.0]])]})]);}
            var Q1;
            Q1=makeQuery(id+"F5.boolean.opBoolean","SPLIT",FACE,{"disambiguationData":[TD([makeQuery(id+"F5.opExtrude","SWEPT_FACE",FACE,{"disambiguationData":[OSD([sQuery(id+"F4.wireOp",EDGE,"E41")])]})])],"derivedFrom":makeQuery(id+"F3.boolean.opBoolean","COPY",FACE,{"derivedFrom":makeQuery(id+"F3.opExtrude","CAP_FACE",FACE,{"disambiguationData":[OSD([sQuery(id+"F0.wireOp",EDGE,"E25.0"),sQuery(id+"F0.wireOp",EDGE,"E25.1"),sQuery(id+"F0.wireOp",EDGE,"E25.2"),sQuery(id+"F0.wireOp",EDGE,"E25.3"),sQuery(id+"F0.wireOp",EDGE,"E25.4"),sQuery(id+"F0.wireOp",EDGE,"E25.5"),sQuery(id+"F0.wireOp",EDGE,"E25.6"),sQuery(id+"F0.wireOp",EDGE,"E25.7")])],"isStart":false})})});
            extrude(context, id + "F13", {"entities" : qUnion([Q0]), "operationType" : NewBodyOperationType.REMOVE, "endBound" : BoundingType.UP_TO_SURFACE, "endBoundEntityFace" : qUnion([Q1]), "depth" : 25 * mm});
        }
        {
            var Q0;
            Q0=makeQuery(id+"F3.boolean.opBoolean","COPY",EDGE,{"derivedFrom":makeQuery(id+"F3.opExtrude","CAP_EDGE",EDGE,{"disambiguationData":[OSD([sQuery(id+"F0.wireOp",EDGE,"E25.6")])],"isStart":false})});
            var Q1;
            Q1=makeQuery(id+"F8.boolean.opBoolean","INTERSECT",EDGE,{"derivedFrom":[makeQuery(id+"F5.opExtrude","SWEPT_FACE",FACE,{"disambiguationData":[OSD([sQuery(id+"F4.wireOp",EDGE,"E30")])]}),makeQuery(id+"F8.opExtrude","CAP_FACE",FACE,{"disambiguationData":[OSD([sQuery(id+"F7.wireOp",EDGE,"E67")])],"isStart":false})]});
            var Q2;
            Q2=makeQuery(id+"F8.boolean.opBoolean","INTERSECT",EDGE,{"disambiguationData":[OD(1.0)],"derivedFrom":[makeQuery(id+"F5.opExtrude","SWEPT_FACE",FACE,{"disambiguationData":[OSD([sQuery(id+"F4.wireOp",EDGE,"E30")])]}),makeQuery(id+"F8.opExtrude","SWEPT_FACE",FACE,{"disambiguationData":[OSD([sQuery(id+"F7.wireOp",EDGE,"E67")])]})]});
            var Q3;
            {var subQ0=sQuery(id+"F4.wireOp",EDGE,"E30");Q3=makeQuery(id+"F8.boolean.opBoolean","SPLIT",EDGE,{"disambiguationData":[TD([makeQuery(id+"F5.opExtrude","SWEPT_FACE",FACE,{"disambiguationData":[OSD([sQuery(id+"F4.wireOp",EDGE,"E35.filletArc")])]})])],"derivedFrom":makeQuery(id+"F5.opExtrude","CAP_EDGE",EDGE,{"disambiguationData":[OSD([subQ0])],"isStart":false})});}
            var Q4;
            {var subQ0=sQuery(id+"F0.wireOp",EDGE,"E25.7");var subQ1=sQuery(id+"F0.wireOp",EDGE,"E25.1");var subQ2=sQuery(id+"F0.wireOp",EDGE,"E25.6");var subQ3=sQuery(id+"F0.wireOp",EDGE,"E25.5");var subQ4=sQuery(id+"F0.wireOp",EDGE,"E25.4");var subQ5=sQuery(id+"F0.wireOp",EDGE,"E25.0");var subQ6=sQuery(id+"F0.wireOp",EDGE,"E25.2");var subQ7=sQuery(id+"F0.wireOp",EDGE,"E25.3");Q4=makeQuery(id+"F8.boolean.opBoolean","INTERSECT",EDGE,{"derivedFrom":[makeQuery(id+"F5.boolean.opBoolean","SPLIT",FACE,{"disambiguationData":[TD([makeQuery(id+"F2.opExtrude","SWEPT_FACE",FACE,{"disambiguationData":[OSD([subQ5])]})])],"derivedFrom":makeQuery(id+"F3.boolean.opBoolean","COPY",FACE,{"derivedFrom":makeQuery(id+"F3.opExtrude","CAP_FACE",FACE,{"disambiguationData":[OSD([subQ5,subQ1,subQ6,subQ7,subQ4,subQ3,subQ2,subQ0])],"isStart":false})})}),makeQuery(id+"F8.opExtrude","SWEPT_FACE",FACE,{"disambiguationData":[OSD([sQuery(id+"F7.wireOp",EDGE,"E67")])]})]});}
            var Q5;
            Q5=makeQuery(id+"F8.boolean.opBoolean","INTERSECT",EDGE,{"disambiguationData":[OD(0.0)],"derivedFrom":[makeQuery(id+"F5.opExtrude","SWEPT_FACE",FACE,{"disambiguationData":[OSD([sQuery(id+"F4.wireOp",EDGE,"E30")])]}),makeQuery(id+"F8.opExtrude","SWEPT_FACE",FACE,{"disambiguationData":[OSD([sQuery(id+"F7.wireOp",EDGE,"E67")])]})]});
            fillet(context, id + "F14", {"entities" : qUnion([Q0, Q1, Q2, Q3, Q4, Q5]), "radius" : 3 * mm, "tangentPropagation" : true, "allowEdgeOverflow" : false});
        }
        {
            var Q0;
            Q0=makeQuery(id+"F1.opExtrude","CAP_EDGE",EDGE,{"disambiguationData":[OSD([sQuery(id+"F0.wireOp",EDGE,"E1.bottom")])],"isStart":false});
            fillet(context, id + "F15", {"entities" : qUnion([Q0]), "radius" : 2 * mm, "tangentPropagation" : true, "allowEdgeOverflow" : false});
        }
        {
            var Q0;
            {var subQ0=sQuery(id+"F0.wireOp",EDGE,"E21.filletArc");var subQ1=sQuery(id+"F0.wireOp",EDGE,"E7");var subQ2=sQuery(id+"F0.wireOp",EDGE,"E6");var subQ3=sQuery(id+"F0.wireOp",EDGE,"E5");var subQ4=sQuery(id+"F0.wireOp",EDGE,"E4");var subQ5=sQuery(id+"F0.wireOp",EDGE,"E22.filletArc");var subQ6=sQuery(id+"F0.wireOp",EDGE,"E1.bottom");var subQ7=sQuery(id+"F0.wireOp",EDGE,"E1.right");var subQ8=sQuery(id+"F0.wireOp",EDGE,"E1.top");var subQ9=sQuery(id+"F0.wireOp",EDGE,"E1.left");var subQ10=sQuery(id+"F0.wireOp",EDGE,"E23.filletArc");var subQ11=sQuery(id+"F0.wireOp",EDGE,"E24.filletArc");Q0=makeQuery(id+"F2.boolean.opBoolean","SPLIT",FACE,{"disambiguationData":[TD([makeQuery(id+"F1.opExtrude","SWEPT_FACE",FACE,{"disambiguationData":[OSD([subQ6])]})])],"derivedFrom":makeQuery(id+"F1.opExtrude","CAP_FACE",FACE,{"disambiguationData":[OSD([subQ6,subQ8,subQ9,subQ7,subQ4,subQ3,subQ2,subQ1,subQ0,subQ5,subQ10,subQ11])],"isStart":true})});}
            var sketch = newSketch(context, id + "F16", { "sketchPlane" : qUnion([Q0])});
            skPoint(sketch, "E79.end.orphan", {"position": v(-26.03, 90) * mm});
            skPoint(sketch, "E80.start.orphan", {"position": v(0, 90) * mm});
            skLineSegment(sketch, "E81", {"start": v(0, 90) * mm, "end": v(0, 120) * mm, "construction": true});
            skCircle(sketch, "E82", {"center": v(0, 120) * mm, "radius": 6 * mm});
            skArc(sketch, "E83", {"start": v(15, 120) * mm, "mid": v(0, 135.03) * mm, "end": v(-15, 120) * mm});
            skLineSegment(sketch, "E84", {"start": v(-15, 120) * mm, "end": v(-14.97, 108) * mm});
            skLineSegment(sketch, "E85", {"start": v(15, 120) * mm, "end": v(15, 108) * mm});
            skLineSegment(sketch, "E86", {"start": v(-14.97, 108) * mm, "end": v(-32.97, 90) * mm});
            skLineSegment(sketch, "E87", {"start": v(15, 108) * mm, "end": v(33, 90) * mm});
            skLineSegment(sketch, "E88", {"start": v(0, 0) * mm, "end": v(-80, 0) * mm, "construction": true});
            skLineSegment(sketch, "E89", {"start": v(0, 0) * mm, "end": v(80, 0) * mm, "construction": true});
            skLineSegment(sketch, "E90.MirrorCS", {"start": v(-14.97, -108) * mm, "end": v(-32.97, -90) * mm});
            skLineSegment(sketch, "E91.MirrorCS", {"start": v(-15, -120) * mm, "end": v(-14.97, -108) * mm});
            skLineSegment(sketch, "E92.MirrorCS", {"start": v(15, -120) * mm, "end": v(15, -108) * mm});
            skLineSegment(sketch, "E93.MirrorCS", {"start": v(15, -108) * mm, "end": v(33, -90) * mm});
            skArc(sketch, "E94.MirrorCS", {"start": v(15, -120) * mm, "mid": v(0, -135.03) * mm, "end": v(-15, -120) * mm});
            skCircle(sketch, "E95.MirrorC", {"center": v(0, -120) * mm, "radius": 6 * mm});
            skLineSegment(sketch, "E96.MirrorCS", {"start": v(0, -90) * mm, "end": v(0, -120) * mm, "construction": true});
            skSolve(sketch);
        }
        {
            var Q0;
            Q0=makeQuery(id+"F16.imprint","IMPRINT",FACE,{"disambiguationData":[TD([[makeQuery(id+"F16.imprint","IMPRINT",EDGE,{"derivedFrom":sQuery(id+"F16.wireOp",EDGE,"E82")}),-1.0]])]});
            var Q1;
            {var subQ1=sQuery(id+"F16.wireOp",EDGE,"E90.MirrorCS");Q1=makeQuery(id+"F16.imprint","IMPRINT",FACE,{"disambiguationData":[TD([[makeQuery(id+"F16.imprint","IMPRINT",EDGE,{"derivedFrom":subQ1}),-1.0]])]});}
            var Q2;
            Q2=makeQuery(id+"F16.imprint","IMPRINT",FACE,{"disambiguationData":[TD([[makeQuery(id+"F16.imprint","IMPRINT",EDGE,{"derivedFrom":makeQuery(id+"F1.opExtrude","CAP_EDGE",EDGE,{"disambiguationData":[OSD([sQuery(id+"F0.wireOp",EDGE,"E1.left")])],"isStart":true})}),-1.0]])]});
            var Q3;
            Q3=makeQuery(id+"F2.opExtrude","CAP_FACE",FACE,{"disambiguationData":[OSD([sQuery(id+"F0.wireOp",EDGE,"E12"),sQuery(id+"F0.wireOp",EDGE,"E13"),sQuery(id+"F0.wireOp",EDGE,"E14"),sQuery(id+"F0.wireOp",EDGE,"E15"),sQuery(id+"F0.wireOp",EDGE,"E17.filletArc"),sQuery(id+"F0.wireOp",EDGE,"E18.filletArc"),sQuery(id+"F0.wireOp",EDGE,"E19.filletArc"),sQuery(id+"F0.wireOp",EDGE,"E20.filletArc"),sQuery(id+"F0.wireOp",EDGE,"E25.0"),sQuery(id+"F0.wireOp",EDGE,"E25.1"),sQuery(id+"F0.wireOp",EDGE,"E25.2"),sQuery(id+"F0.wireOp",EDGE,"E25.3"),sQuery(id+"F0.wireOp",EDGE,"E25.4"),sQuery(id+"F0.wireOp",EDGE,"E25.5"),sQuery(id+"F0.wireOp",EDGE,"E25.6"),sQuery(id+"F0.wireOp",EDGE,"E25.7")])],"isStart":false});
            extrude(context, id + "F17", {"entities" : qUnion([Q0, Q1, Q2]), "endBound" : BoundingType.UP_TO_SURFACE, "endBoundEntityFace" : qUnion([Q3]), "depth" : 25 * mm});
        }
    });
